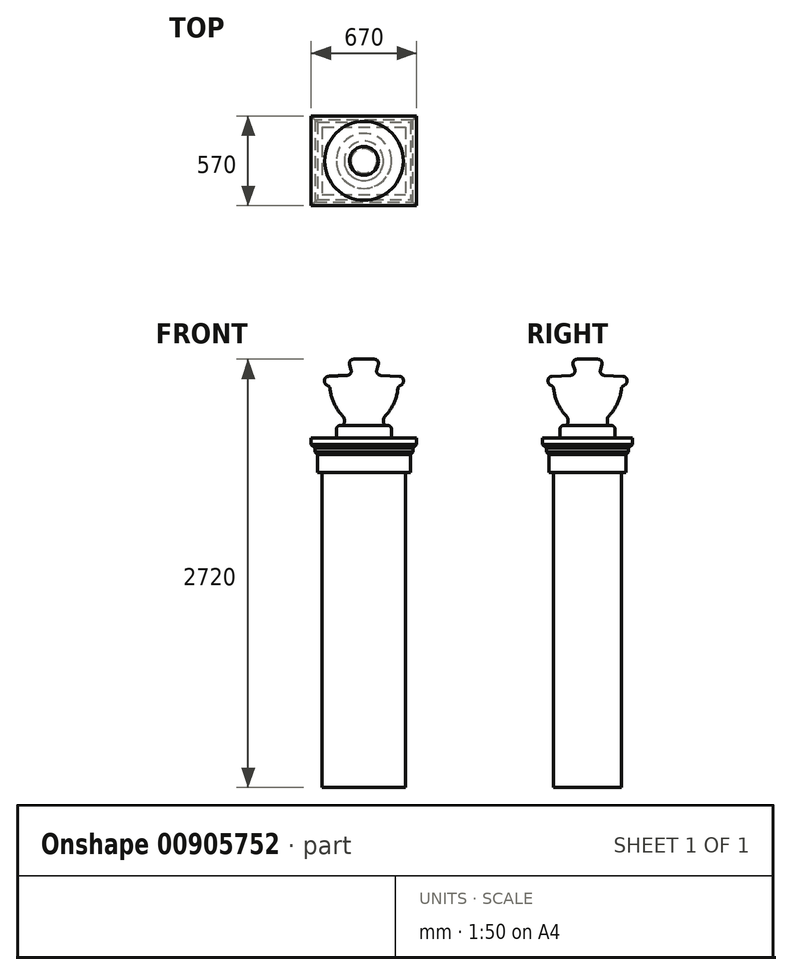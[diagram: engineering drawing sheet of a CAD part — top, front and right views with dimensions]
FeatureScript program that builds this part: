
annotation { "Feature Type Name" : "Feature", "Feature Type Description" : "" }
export const myFeature = defineFeature(function(context is Context, id is Id, definition is map)
    precondition{}
    {
        {
            var Q0;
            Q0=qCreatedBy(makeId("Top.planeOp"),FACE);
            var sketch = newSketch(context, id + "F0", { "sketchPlane" : qUnion([Q0])});
            skLineSegment(sketch, "E0.bottom", {"start": v(-265, 215) * mm, "end": v(265, 215) * mm});
            skLineSegment(sketch, "E0.top", {"start": v(-265, -215) * mm, "end": v(265, -215) * mm});
            skLineSegment(sketch, "E0.left", {"start": v(-265, 215) * mm, "end": v(-265, -215) * mm});
            skLineSegment(sketch, "E0.right", {"start": v(265, 215) * mm, "end": v(265, -215) * mm});
            skSolve(sketch);
        }
        {
            var Q0;
            Q0=qSketchRegion(id+"F0",true);
            extrude(context, id + "F1", {"entities" : qUnion([Q0]), "depth" : 2000 * mm, "offsetDistance" : 25.4 * mm});
        }
        {
            var Q0;
            Q0=makeQuery(id+"F1.opExtrude","CAP_FACE",FACE,{"disambiguationData":[OSD([sQuery(id+"F0.wireOp",EDGE,"E0.bottom"),sQuery(id+"F0.wireOp",EDGE,"E0.top"),sQuery(id+"F0.wireOp",EDGE,"E0.left"),sQuery(id+"F0.wireOp",EDGE,"E0.right")])],"isStart":false});
            var sketch = newSketch(context, id + "F2", { "sketchPlane" : qUnion([Q0])});
            skLineSegment(sketch, "E1.bottom", {"start": v(-295, 245) * mm, "end": v(295, 245) * mm});
            skLineSegment(sketch, "E1.top", {"start": v(-295, -245) * mm, "end": v(295, -245) * mm});
            skLineSegment(sketch, "E1.left", {"start": v(-295, 245) * mm, "end": v(-295, -245) * mm});
            skLineSegment(sketch, "E1.right", {"start": v(295, 245) * mm, "end": v(295, -245) * mm});
            skSolve(sketch);
        }
        {
            var Q0;
            Q0=qSketchRegion(id+"F2",true);
            extrude(context, id + "F3", {"entities" : qUnion([Q0]), "operationType" : NewBodyOperationType.ADD, "depth" : 100 * mm, "offsetDistance" : 25.4 * mm});
        }
        {
            var Q0;
            Q0=qCreatedBy(makeId("Right.planeOp"),FACE);
            var sketch = newSketch(context, id + "F4", { "sketchPlane" : qUnion([Q0])});
            skLineSegment(sketch, "E2.0", {"start": v(-245, 2100) * mm, "end": v(-245, 2000) * mm, "construction": true});
            skLineSegment(sketch, "E3.0", {"start": v(245, 2100) * mm, "end": v(-245, 2100) * mm, "construction": true});
            skLineSegment(sketch, "E4", {"start": v(-245, 2100) * mm, "end": v(-245, 2115) * mm});
            skLineSegment(sketch, "E5", {"start": v(-245, 2115) * mm, "end": v(-260, 2130) * mm});
            skLineSegment(sketch, "E6", {"start": v(-260, 2130) * mm, "end": v(-260, 2155) * mm});
            skLineSegment(sketch, "E7", {"start": v(-260, 2155) * mm, "end": v(-285, 2180) * mm});
            skLineSegment(sketch, "E8", {"start": v(-285, 2180) * mm, "end": v(-285, 2220) * mm});
            skLineSegment(sketch, "E9", {"start": v(-285, 2220) * mm, "end": v(-205, 2220) * mm});
            skLineSegment(sketch, "E10", {"start": v(-245, 2100) * mm, "end": v(-205, 2100) * mm});
            skLineSegment(sketch, "E11", {"start": v(-205, 2100) * mm, "end": v(-205, 2220) * mm});
            skPoint(sketch, "E12.orphan", {"position": v(-230, 2220) * mm});
            skSolve(sketch);
        }
        {
            var Q0;
            Q0=qSketchRegion(id+"F4",true);
            var Q1;
            Q1=makeQuery(id+"F3.opExtrude","CAP_EDGE",EDGE,{"disambiguationData":[OSD([sQuery(id+"F2.wireOp",EDGE,"E1.top")])],"isStart":false});
            var Q2;
            Q2=makeQuery(id+"F3.opExtrude","CAP_EDGE",EDGE,{"disambiguationData":[OSD([sQuery(id+"F2.wireOp",EDGE,"E1.right")])],"isStart":false});
            var Q3;
            Q3=makeQuery(id+"F3.opExtrude","CAP_EDGE",EDGE,{"disambiguationData":[OSD([sQuery(id+"F2.wireOp",EDGE,"E1.bottom")])],"isStart":false});
            var Q4;
            Q4=makeQuery(id+"F3.opExtrude","CAP_EDGE",EDGE,{"disambiguationData":[OSD([sQuery(id+"F2.wireOp",EDGE,"E1.left")])],"isStart":false});
            sweep(context, id + "F5", {"profiles" : qUnion([Q0]), "path" : qUnion([Q1, Q2, Q3, Q4])});
        }
        {
            var Q0;
            Q0=makeQuery(id+"F5.opSweep","SWEPT_FACE",FACE,{"disambiguationData":[OSD([sQuery(id+"F2.wireOp",EDGE,"E1.right"),sQuery(id+"F4.wireOp",EDGE,"E9")])]});
            var sketch = newSketch(context, id + "F6", { "sketchPlane" : qUnion([Q0])});
            skLineSegment(sketch, "E13.0", {"start": v(-255, 205) * mm, "end": v(-255, -205) * mm});
            skLineSegment(sketch, "E14.0", {"start": v(-255, -205) * mm, "end": v(255, -205) * mm});
            skLineSegment(sketch, "E15.0", {"start": v(255, -205) * mm, "end": v(255, 205) * mm});
            skLineSegment(sketch, "E16.0", {"start": v(255, 205) * mm, "end": v(-255, 205) * mm});
            skSolve(sketch);
        }
        {
            var Q0;
            Q0=qSketchRegion(id+"F6",true);
            var Q1;
            Q1=makeQuery(id+"F3.opExtrude","CAP_FACE",FACE,{"disambiguationData":[OSD([sQuery(id+"F2.wireOp",EDGE,"E1.bottom"),sQuery(id+"F2.wireOp",EDGE,"E1.top"),sQuery(id+"F2.wireOp",EDGE,"E1.left"),sQuery(id+"F2.wireOp",EDGE,"E1.right")])],"isStart":false});
            var Q2;
            Q2=makeQuery(id+"F5.opSweep","MID_CAP_VERTEX",VERTEX,{"disambiguationData":[OSD([sQuery(id+"F2.wireOp",EDGE,"E1.bottom"),sQuery(id+"F4.wireOp",EDGE,"E10"),sQuery(id+"F4.wireOp",EDGE,"E11")])],"capPos":2.0});
            extrude(context, id + "F7", {"entities" : qUnion([Q0]), "operationType" : NewBodyOperationType.ADD, "endBound" : BoundingType.UP_TO_SURFACE, "oppositeDirection" : true, "depth" : 25.4 * mm, "endBoundEntityFace" : qUnion([Q1]), "endBoundEntityVertex" : qUnion([Q2]), "offsetDistance" : 25.4 * mm});
        }
        {
            var Q0;
            Q0=qCreatedBy(makeId("Right.planeOp"),FACE);
            var sketch = newSketch(context, id + "F8", { "sketchPlane" : qUnion([Q0])});
            skLineSegment(sketch, "E17", {"start": v(0, 0) * mm, "end": v(0, 2720) * mm, "construction": true});
            skLineSegment(sketch, "E18.0", {"start": v(-285, 2220) * mm, "end": v(285, 2220) * mm, "construction": true});
            skLineSegment(sketch, "E19", {"start": v(0, 2720) * mm, "end": v(100, 2720) * mm});
            skLineSegment(sketch, "E20", {"start": v(100, 2720) * mm, "end": v(73.2, 2620) * mm});
            skLineSegment(sketch, "E21", {"start": v(73.2, 2620) * mm, "end": v(250, 2610.73) * mm});
            skLineSegment(sketch, "E22", {"start": v(250, 2610.73) * mm, "end": v(250, 2560.73) * mm});
            skLineSegment(sketch, "E23", {"start": v(250, 2560.73) * mm, "end": v(216.74, 2548.63) * mm});
            skLineSegment(sketch, "E24", {"start": v(0, 2220) * mm, "end": v(175, 2220) * mm});
            skLineSegment(sketch, "E25", {"start": v(175, 2220) * mm, "end": v(175, 2300) * mm});
            skLineSegment(sketch, "E26", {"start": v(175, 2300) * mm, "end": v(125, 2300) * mm});
            skLineSegment(sketch, "E27", {"start": v(125, 2300) * mm, "end": v(125, 2349.12) * mm});
            skArc(sketch, "E28", {"start": v(125, 2349.12) * mm, "mid": v(189.78, 2440.18) * mm, "end": v(216.74, 2548.63) * mm});
            skLineSegment(sketch, "E29", {"start": v(73.2, 2620) * mm, "end": v(128.16, 2620) * mm, "construction": true});
            skLineSegment(sketch, "E30", {"start": v(0, 2720) * mm, "end": v(0, 2220) * mm});
            skSolve(sketch);
        }
        {
            var Q0;
            Q0=qSketchRegion(id+"F8",true);
            var Q1;
            Q1=sQuery(id+"F8.wireOp",EDGE,"E17");
            revolve(context, id + "F9", {"operationType" : NewBodyOperationType.ADD, "surfaceOperationType" : NewSurfaceOperationType.NEW, "entities" : qUnion([Q0]), "axis" : qUnion([Q1]), "revolveType" : RevolveType.FULL});
        }
        {
            var Q0;
            Q0=makeQuery(id+"F9.opRevolve","SWEPT_EDGE",EDGE,{"disambiguationData":[OSD([sQuery(id+"F8.wireOp",EDGE,"E24"),sQuery(id+"F8.wireOp",EDGE,"E25")])]});
            var Q1;
            Q1=makeQuery(id+"F9.opRevolve","SWEPT_EDGE",EDGE,{"disambiguationData":[OSD([sQuery(id+"F8.wireOp",EDGE,"E25"),sQuery(id+"F8.wireOp",EDGE,"E26")])]});
            var Q2;
            Q2=makeQuery(id+"F9.opRevolve","SWEPT_EDGE",EDGE,{"disambiguationData":[OSD([sQuery(id+"F8.wireOp",EDGE,"E27"),sQuery(id+"F8.wireOp",EDGE,"E28")])]});
            var Q3;
            Q3=makeQuery(id+"F9.opRevolve","SWEPT_EDGE",EDGE,{"disambiguationData":[OSD([sQuery(id+"F8.wireOp",EDGE,"E23"),sQuery(id+"F8.wireOp",EDGE,"E28")])]});
            var Q4;
            Q4=makeQuery(id+"F9.opRevolve","SWEPT_EDGE",EDGE,{"disambiguationData":[OSD([sQuery(id+"F8.wireOp",EDGE,"E20"),sQuery(id+"F8.wireOp",EDGE,"E21")])]});
            var Q5;
            Q5=makeQuery(id+"F9.opRevolve","SWEPT_EDGE",EDGE,{"disambiguationData":[OSD([sQuery(id+"F8.wireOp",EDGE,"E22"),sQuery(id+"F8.wireOp",EDGE,"E23")])]});
            var Q6;
            Q6=makeQuery(id+"F9.opRevolve","SWEPT_EDGE",EDGE,{"disambiguationData":[OSD([sQuery(id+"F8.wireOp",EDGE,"E21"),sQuery(id+"F8.wireOp",EDGE,"E22")])]});
            var Q7;
            Q7=makeQuery(id+"F9.opRevolve","SWEPT_EDGE",EDGE,{"disambiguationData":[OSD([sQuery(id+"F8.wireOp",EDGE,"E19"),sQuery(id+"F8.wireOp",EDGE,"E20")])]});
            fillet(context, id + "F10", {"entities" : qUnion([Q0, Q1, Q2, Q3, Q4, Q5, Q6, Q7]), "radius" : 25.4 * mm, "tangentPropagation" : true, "allowEdgeOverflow" : false});
        }
        {
            var Q0;
            Q0=makeQuery(id+"F9.opRevolve","SWEPT_EDGE",EDGE,{"disambiguationData":[OSD([sQuery(id+"F8.wireOp",EDGE,"E26"),sQuery(id+"F8.wireOp",EDGE,"E27")])]});
            fillet(context, id + "F11", {"entities" : qUnion([Q0]), "radius" : 19.05 * mm, "tangentPropagation" : true, "allowEdgeOverflow" : false});
        }
    });
